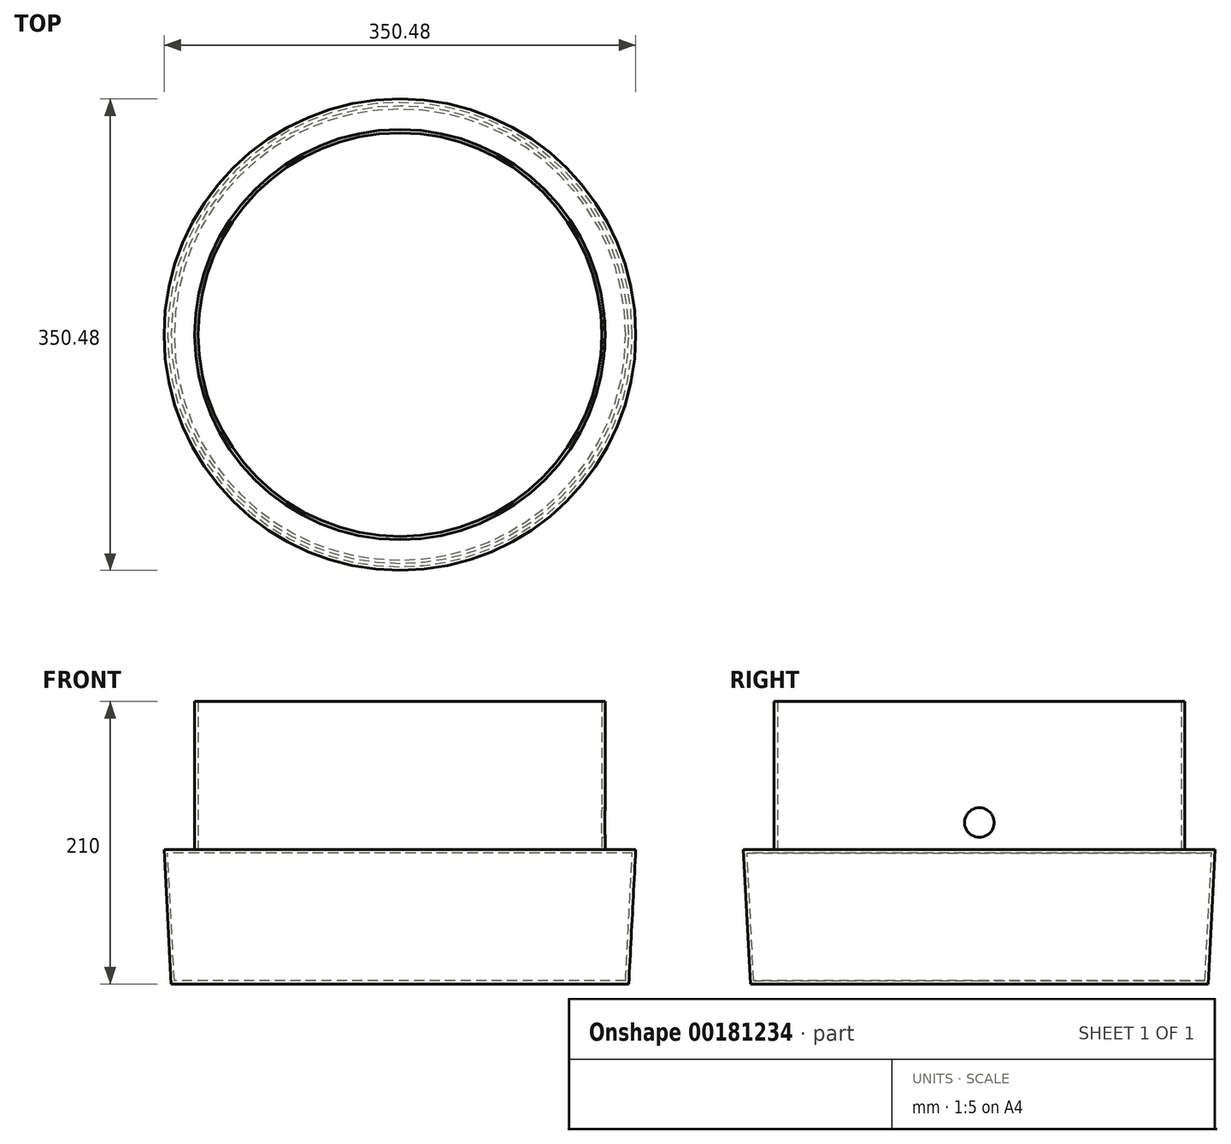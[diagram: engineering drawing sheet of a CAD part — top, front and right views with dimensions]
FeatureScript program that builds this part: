
annotation { "Feature Type Name" : "Feature", "Feature Type Description" : "" }
export const myFeature = defineFeature(function(context is Context, id is Id, definition is map)
    precondition{}
    {
        {
            var Q0;
            Q0=qCreatedBy(makeId("Top.planeOp"),FACE);
            var sketch = newSketch(context, id + "F0", { "sketchPlane" : qUnion([Q0])});
            skCircle(sketch, "E0", {"center": v(0, 0) * mm, "radius": 170 * mm});
            skSolve(sketch);
        }
        {
            var Q0;
            Q0 = qSketchRegion(id + "F0", true);
            extrude(context, id + "F1", {"entities" : qUnion([Q0]), "depth" : 100 * mm, "hasDraft" : true, "draftAngle" : 3 * degree});
        }
        {
            var Q0;
            Q0=makeQuery(id+"F1.opExtrude","CAP_FACE",FACE,{"disambiguationData":[OSD([sQuery(id+"F0.wireOp",EDGE,"E0")])],"isStart":false});
            var sketch = newSketch(context, id + "F7", { "sketchPlane" : qUnion([Q0])});
            skCircle(sketch, "E1", {"center": v(0, 0) * mm, "radius": 152.5 * mm});
            skSolve(sketch);
        }
        {
            var Q0;
            Q0=makeQuery(id+"F7.imprint","IMPRINT",FACE,{"disambiguationData":[TD([[makeQuery(id+"F7.imprint","IMPRINT",EDGE,{"derivedFrom":sQuery(id+"F7.wireOp",EDGE,"E1")}),1.0]])]});
            extrude(context, id + "F2", {"entities" : qUnion([Q0]), "operationType" : NewBodyOperationType.ADD, "depth" : 110 * mm});
        }
        {
            var Q0;
            Q0=qCreatedBy(makeId("Right.planeOp"),FACE);
            cPlane(context, id + "F3", {"entities" : qUnion([Q0]), "cplaneType" : CPlaneType.OFFSET, "offset" : 200 * mm, "width" : 150 * mm, "height" : 150 * mm});
        }
        {
            var Q0;
            Q0=makeQuery(id+"F2.opExtrude","CAP_FACE",FACE,{"disambiguationData":[OSD([sQuery(id+"F7.wireOp",EDGE,"E1")])],"isStart":false});
            shell(context, id + "F4", {"entities" : qUnion([Q0]), "thickness" : 2.5 * mm});
        }
        {
            var Q0;
            Q0=qCreatedBy(id+"F3.planeOp",FACE);
            var sketch = newSketch(context, id + "F5", { "sketchPlane" : qUnion([Q0])});
            skPoint(sketch, "E2", {"position": v(0, 120) * mm});
            skSolve(sketch);
        }
        {
            var Q0;
            Q0=sQuery(id+"F5.wireOp",VERTEX,"E2");
            var Q1;
            Q1=makeQuery(id+"F1.opExtrude","SWEPT_BODY",BODY,{"disambiguationData":[OSD([sQuery(id+"F0.wireOp",EDGE,"E0")])]});
            hole(context, id + "F6", {"style" : HoleStyle.SIMPLE, "endStyle" : HoleEndStyle.BLIND, "holeDiameter" : 22 * mm, "holeDepth" : 200 * mm, "locations" : qUnion([Q0]), "scope" : qUnion([Q1])});
        }
    });
